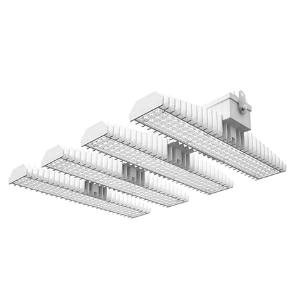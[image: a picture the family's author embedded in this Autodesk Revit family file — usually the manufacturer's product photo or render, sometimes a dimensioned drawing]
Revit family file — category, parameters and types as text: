
# Revit family: 3f_filippi_-_3f_lem_ampio_3f_filippi_-_58884_a0811_-_3f_lem_4_led_200_cr_ampio___vt_4f80
name_source: partatom
category: Lighting Fixtures
units: mm (PartAtom-declared; Revit-internal decimal feet)

## family parameters
Cut with Voids When Loaded = No
Host = Face
Light Source = No
Part Type = Normal
Room Calculation Point = No
Round Connector Dimension = Use Diameter
Shared = No

## types (1)
- 3F Filippi - 3F LEM Ampio (1 x LED, 31641 lm, 218 W, 4000 K)
    Apparent Load = 218 VA
    Approval mark = CE
    CIE Flux Codes = 60 92 99 100 100
    Color Rendering = 80
    Color Temperature = 4000 K
    Control Gear = Electronic ballast
    Default Elevation = 1800 mm
    Description = Industrial luminaire with high light output and high luminous efficiency designed with the most innovative technologies for environments with temperature up to 55°C.

ILLUMINOTECHNICAL
Luminous efficiency 100% (DLOR 99%, ULOR 1%).
Initial luminous flux of the luminaire 31641 lm.
Direct symmetric wide distribution: the illuminated area has a rectangular shape.
Installation Interdistance Transv.D = 1.58 x hu - Long.D = 1.45 x hu.
Tabular UGR (CIE 117 - 4H-8H; S=0.25H; 70/50/20): RUG 22.9 - 23.9.
Beam angle: 93° - 99°.
Luminous efficacy 145 lm/W.
Lifetime (L93/B10): 30000 h. (tq+25°C)
Lifetime (L90/B10): 50000 h. (tq+25°C)
Lifetime (L85/B10): 80000 h. (tq+25°C)
Lifetime (L80/B10): 100000 h. (tq+25°C)
Lifetime (L85/B10): 50000 h. (tq+55°C)
Sudden decreased luminous flux after 50000 hours: 0% (C0).
Photobiological safety in compliance with IEC/TR 62778: RG0 risk exempt, (IEC 62471).
In compliance with IEC/EN 62722-2-1 - IEC/EN 62717 standards.

SOURCE
4 Mid-Power linear LED modules 50W/840.
Energy efficiency class (UE 2019/2020 - UE 2019/2015): C.
CIE 13.3 Colour rendering index: CRI >80 (R9 <50%).
IES TM-30 Fidelity Index: Rf = 84 Rg = 95.
CCT nominal colour temperature 4000 K.
Colour initial tolerance (MacAdam): SDCM 3.

MECHANICAL
Passive modular heatsinks in die-casted aluminium, painted in white colour.
To optimize the thermal management of the LED module, the heatsinks are oversized and provided with self-cleaning of cooling fins.
Wiring body in aluminium and galvanised steel anchored solidly to the sinks and thermally separated.
3F Lens lenses with high luminous efficiency, transparent methacrylate (PMMA), fixed to the LED modules.
Fixing brackets in stainless steel.
Luminaire with limited surface temperature. - D - (EN 60598-2-24)
Dimensions: 757x542 mm, height 133 mm. Weight 19.353 kg.
IP65 protection degree.
Mechanical strength to impacts IK06 (1 joule).
Glow-wire test resistance 650°C.

ELECTRICAL
Halogen Free electronic wiring 230V-50/60Hz, power factor 0.97, THD <25%, constant output current, class I, 2 driver.
Power of the luminaire 218 W.
ENEC - CE.
SAFE FLICKER: PstLM=<1 and SVM=<0.4 (IEC TR 61547-1 and IEC TR 63158), to ensure a more comfortable and safe light.
Luminaire compliant with EN 60598-2-22 for power supply from a centralised emergency system CPSS (Central Power Supply System), not incorporated in the luminaire - high risk areas excluded. The default power and flux are 100% in AC and 100% in DC.
Ambient temperature from -30°C to +55°C.
Temperature class T6 max 85°C.
Quick connection via M20 3P connector with 9-13 mm tightening range.
Power unit positioned on a separate compartment by the LED module to ensure optimum temperatures of cabling components, to be inspectable and maintainable.
Relative humidity UR: <85%.

INSTALLATION
Ceiling / Suspended / Wall.
All accessories dedicated to this product are available on the Catalog and on our website www.3F-Filippi.com.

ACCESSORIES
A0811 - VT transparent glass, tempered, not flammable, with sealing gasket.
One required for each light module. The pack contains 10 pieces.

APPLICATIONS
In commercial environments, exhibition and industrial areas, stores, open areas.
Applications with high ambient temperature up to 55°C.
Environments in which it is necessary a total protection against falling fragments (eg environments with foodstuffs or machines with moving parts or with extreme temperature changes), use luminaires with polycarbonate lenses.

WARNING
Fixture not suitable for cold stores with an ambient temperature <0°C and/or relative humidity >85%.
Luminaire designed for disposal/recycling at end-of-life.
Replaceable (LED only) light source by a professional. Replaceable control gear by a professional.
    Height = 133 mm  [stored 0.436352 ft]
    Lamp = 1 x LED
    Lamp Light Flux = 31641 lm
    Lamp Power = 218 W
    Lamp count = 1
    Length = 757 mm
    Lifetime = 50000 h
    Luminous efficacy = 145 lm/W
    Manufacturer = 3F Filippi
    ModVariant = No
    Model = 3F Filippi - 58884+A0811 - 3F LEM 4 LED 200 CR AMPIO + VT
    Mounting Place = Ceiling
    Mounting Type = Pendant
    Number of Poles = 1
    OnlyDefault = Yes
    Power Factor = 1
    Product Name = 3F Filippi - 3F LEM Ampio
    Product group = pendant luminaire
    ProductGroupID = 9
    Protection Class = Protection class I
    Protection Degree = IP 65
    RLX_Detail_Level = 1
    RLX_Emergency_Light_Flux = 0 lm
    RLX_Emergency_Type = 0
    RLX_Emergency_Type_DB = No
    RlxData = <blob elided: 118333 chars, md5=3ef9da88>
    Socket = socket
    Standby Power = 0 W
    System Light Flux = 31641 lm
    System Power = 218 W
    Type Comments = Product without accessories
    Type Image = 3f_filippi_-_lem_4__a0811.jpg
    URL = http://relux.com
    VarID = ---
    Voltage = 0 V
    Weight = 0.00 kg
    Width = 542 mm

note: [stored X ft] marks values corroborated as IEEE doubles in the binary element streams (Revit-internal decimal feet)

## geometry (parser evidence)
native form markers: Blend x4, Sweep x14
no freeform markers — native parametric forms only
